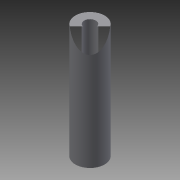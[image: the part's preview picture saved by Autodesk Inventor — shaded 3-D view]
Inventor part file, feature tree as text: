
AUTODESK INVENTOR PART (.ipt)
format: ipt  version: 2015 (Build 190159000, 159)  size: 86,016 bytes
history: native  units: in
note: dims shown in document units (in); Inventor stores cm internally (conversion verified against a paired STEP export)
features: extrude x1, sketch x1
ambient origin geometry x8: Origin, YZ Plane, XZ Plane, XY Plane, X Axis, Y Axis, Z Axis, Center Point
bodies: Solid1 (feature_tree)
feature tree (2):
  extrude  "Extrusion1"  Depth=2.75in
  sketch  "Sketch1"  dims[d0=0.625in d1=0.25in d2=2.75in d3=0.0in]
